# Revit family: LeL Ginko 2.0
name_source: partatom
category: Lighting Fixtures
units: mm (PartAtom-declared; Revit-internal decimal feet)

## family parameters
Always vertical = No
Cut with Voids When Loaded = No
Light Source = No
OmniClass Number = 23.80.70.00
OmniClass Title = Lighting
Part Type = Normal
Room Calculation Point = No
Round Connector Dimension = Use Diameter
Shared = No
Work Plane-Based = Yes

## types (23) — shared parameters
CCT = 3000 K
CRI = CRI80
Default Elevation = 1219 mm
Description = Outdoor Projectors
IK = IK07
IP = IP66 - 69
Lamp = LED
Manufacturer = L&L Luce&Light srl
Model = GN20
Rated Power supply = 24 V
URL = https://www.lucelight.it
Weight = 0.41 kg
Weight Brass = 0.91 kg
Weight Stainless steel = 0.83 kg

## per-type parameters (varying)
| type | Apparent Load | Lumen Output | Photometry | Wattage |
| J 47° 5W | 5 VA | 281 lm | GN20 Light source : J 47° 5W | 5 W |
| K 68° 5W | 5 VA | 240 lm | GN20 Light source : K 68° 5W | 5 W |
| L 45° 5W | 5 VA | 283 lm | GN20 Light source : L 45° 5W | 5 W |
| M 34° 5W | 5 VA | 352 lm | GN20 Light source : M 34° 5W | 5 W |
| P (21°) 5W | 5 VA | 245 lm | GN20 Light source : P (21°) 5W | 5 W |
| Q (61°) 5W | 5 VA | 213 lm | GN20 Light source : Q (61°) 5W | 5 W |
| S 17° 5W | 5 VA | 338 lm | GN20 Light source : S 17° 5W | 5 W |
| T 11° 5W | 5 VA | 336 lm | GN20 Light source : T 11° 5W | 5 W |
| W 13°x52° 5W | 5 VA | 316 lm | GN20 Light source : W 13°x52° 5W | 5 W |
| X 54°x15° 5W | 5 VA | 301 lm | GN20 Light source : X 54°x15° 5W | 5 W |
| J 47° 7W | 7 VA | 370 lm | GN20 Light source : J 47° 7W | 7 W |
| V 8° 5W | 5 VA | 344 lm | GN20 Light source : V 8° 5W | 5 W |
| K 68° 7W | 7 VA | 317 lm | GN20 Light source : K 68° 7W | 7 W |
| L 45° 7W | 7 VA | 373 lm | GN20 Light source : L 45° 7W | 7 W |
| M 34° 7W | 7 VA | 463 lm | GN20 Light source : M 34° 7W | 7 W |
| P (21°) 7W | 7 VA | 323 lm | GN20 Light source : P (21°) 7W | 7 W |
| Q (61°) 7W | 7 VA | 281 lm | GN20 Light source : Q (61°) 7W | 7 W |
| S 17° 7W | 7 VA | 446 lm | GN20 Light source : S 17° 7W | 7 W |
| T 11° 7W | 7 VA | 443 lm | GN20 Light source : T 11° 7W | 7 W |
| V 8° 7W | 7 VA | 453 lm | GN20 Light source : V 8° 7W | 7 W |
| W 13°x52° 7W | 7 VA | 416 lm | GN20 Light source : W 13°x52° 7W | 7 W |
| X 54°x15° 7W | 7 VA | 395 lm | GN20 Light source : X 54°x15° 7W | 7 W |
| U 5° 3.5W | 4 VA | 177 lm | GN20 Light source : U 5° 3.5W | 4 W |

## geometry (parser evidence)
native form markers: Sweep x2
no freeform markers — native parametric forms only
